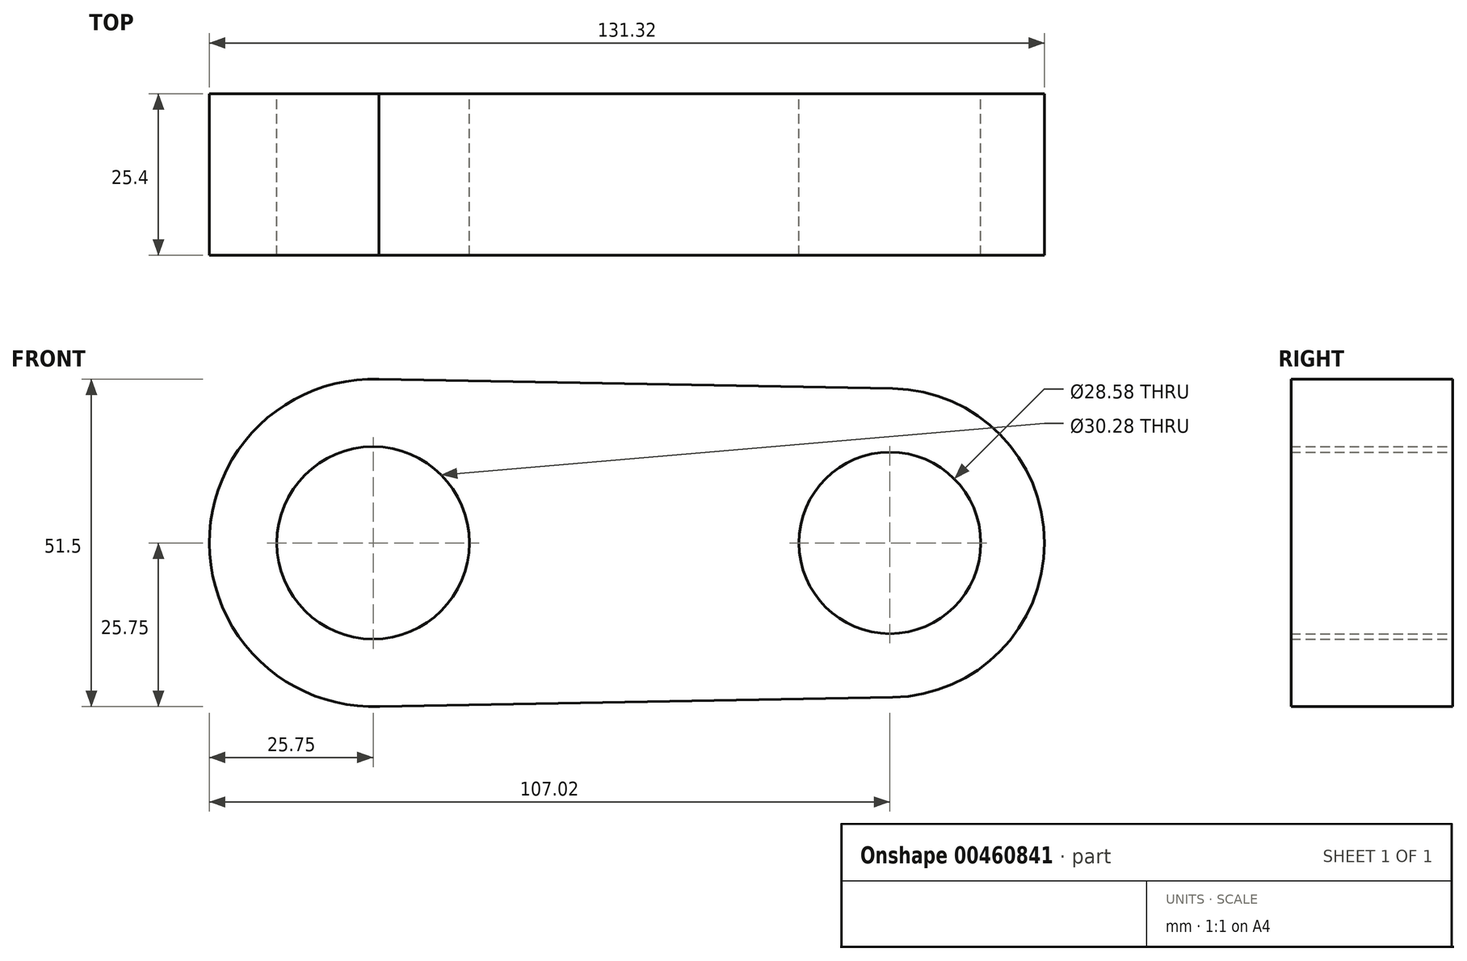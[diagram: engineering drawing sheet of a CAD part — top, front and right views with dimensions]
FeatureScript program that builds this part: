
annotation { "Feature Type Name" : "Feature", "Feature Type Description" : "" }
export const myFeature = defineFeature(function(context is Context, id is Id, definition is map)
    precondition{}
    {
        {
            var Q0;
            Q0=qCreatedBy(makeId("Front.planeOp"),FACE);
            var sketch = newSketch(context, id + "F0", { "sketchPlane" : qUnion([Q0])});
            skCircle(sketch, "E0", {"center": v(0, 0) * mm, "radius": 25.75 * mm});
            skCircle(sketch, "E1", {"center": v(81.27, 0) * mm, "radius": 24.3 * mm});
            skLineSegment(sketch, "E2", {"start": v(0, 25.75) * mm, "end": v(81.7, 24.3) * mm});
            skLineSegment(sketch, "E3", {"start": v(1.04, -25.73) * mm, "end": v(81.7, -24.3) * mm});
            skCircle(sketch, "E4", {"center": v(0, 0) * mm, "radius": 15.14 * mm});
            skCircle(sketch, "E5", {"center": v(81.27, 0) * mm, "radius": 14.29 * mm});
            skSolve(sketch);
        }
        {
            var Q0;
            Q0 = qSketchRegion(id + "F0", true);
            extrude(context, id + "F1", {"entities" : qUnion([Q0]), "depth" : 25.4 * mm});
        }
    });
